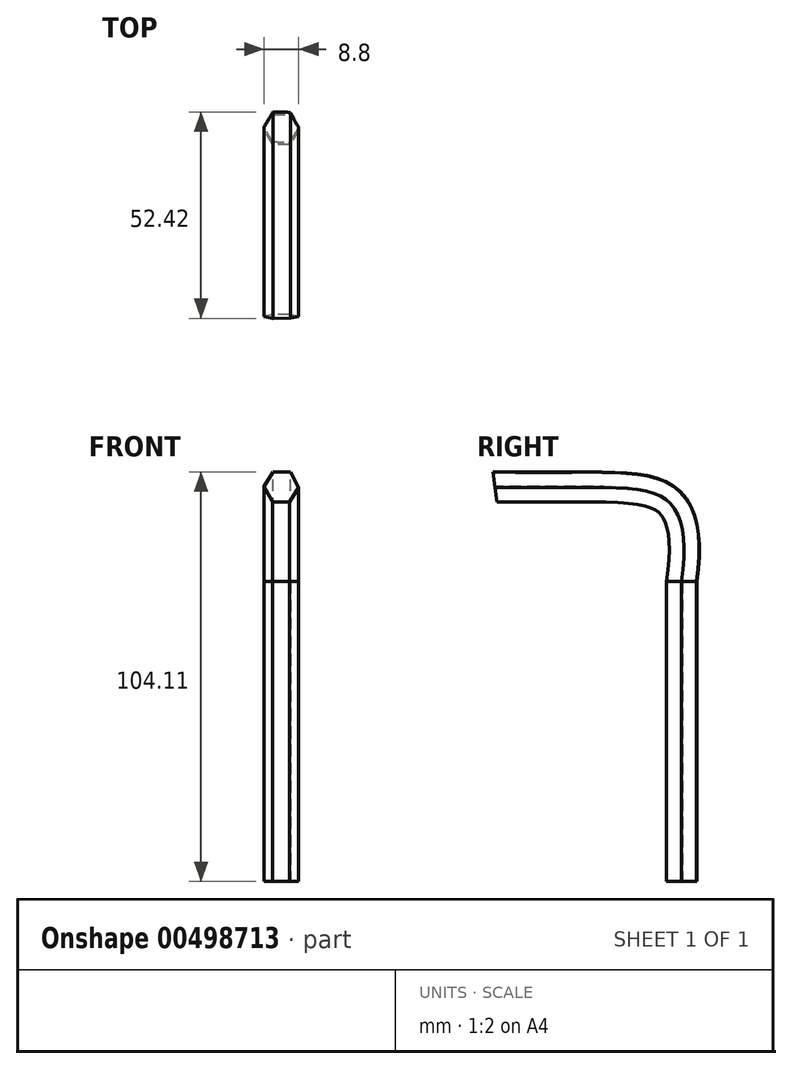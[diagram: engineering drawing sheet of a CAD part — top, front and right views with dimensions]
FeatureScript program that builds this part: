
annotation { "Feature Type Name" : "Feature", "Feature Type Description" : "" }
export const myFeature = defineFeature(function(context is Context, id is Id, definition is map)
    precondition{}
    {
        {
            var Q0;
            Q0=qCreatedBy(makeId("Top.planeOp"),FACE);
            var sketch = newSketch(context, id + "F0", { "sketchPlane" : qUnion([Q0])});
            skCircle(sketch, "E0.cCircle", {"center": v(-8.9, 61.26) * mm, "radius": 3.81 * mm, "construction": true});
            skLineSegment(sketch, "E0.0", {"start": v(-4.5, 61.16) * mm, "end": v(-6.78, 57.4) * mm});
            skLineSegment(sketch, "E0.1", {"start": v(-6.78, 57.4) * mm, "end": v(-11.18, 57.5) * mm});
            skLineSegment(sketch, "E0.2", {"start": v(-11.18, 57.5) * mm, "end": v(-13.29, 61.36) * mm});
            skLineSegment(sketch, "E0.3", {"start": v(-13.29, 61.36) * mm, "end": v(-11, 65.12) * mm});
            skLineSegment(sketch, "E0.4", {"start": v(-11, 65.12) * mm, "end": v(-6.6, 65.02) * mm});
            skLineSegment(sketch, "E0.5", {"start": v(-6.6, 65.02) * mm, "end": v(-4.5, 61.16) * mm});
            skPoint(sketch, "E0.0.midPoint", {"position": v(-5.64, 59.28) * mm});
            skSolve(sketch);
        }
        {
            var Q0;
            Q0 = qSketchRegion(id + "F0", true);
            extrude(context, id + "F1", {"entities" : qUnion([Q0]), "depth" : 76.2 * mm, "offsetDistance" : 25.4 * mm});
        }
        {
            var Q0;
            Q0=qCreatedBy(makeId("Right.planeOp"),FACE);
            var sketch = newSketch(context, id + "F2", { "sketchPlane" : qUnion([Q0])});
            skLineSegment(sketch, "E1.0.0", {"start": v(61.16, 76.2) * mm, "end": v(65.02, 76.2) * mm});
            skLineSegment(sketch, "E1.0.1", {"start": v(65.02, 76.2) * mm, "end": v(65.12, 76.2) * mm});
            skLineSegment(sketch, "E1.0.2", {"start": v(65.12, 76.2) * mm, "end": v(61.36, 76.2) * mm});
            skLineSegment(sketch, "E1.0.3", {"start": v(61.36, 76.2) * mm, "end": v(57.5, 76.2) * mm});
            skLineSegment(sketch, "E1.0.4", {"start": v(57.5, 76.2) * mm, "end": v(57.4, 76.2) * mm});
            skLineSegment(sketch, "E1.0.5", {"start": v(57.4, 76.2) * mm, "end": v(61.16, 76.2) * mm});
            skFitSpline(sketch, "E2", {"points": [v(61.36, 76.2) * mm, v(58.2, 96.52) * mm, v(13.8, 100.38) * mm], "startDerivative": vector(10.48, 74.63) * mm, "endDerivative": vector(-137.11, 1.75) * mm});
            skSolve(sketch);
        }
        {
            var Q0;
            Q0=makeQuery(id+"F1.opExtrude","CAP_FACE",FACE,{"disambiguationData":[OSD([sQuery(id+"F0.wireOp",EDGE,"E0.0"),sQuery(id+"F0.wireOp",EDGE,"E0.1"),sQuery(id+"F0.wireOp",EDGE,"E0.2"),sQuery(id+"F0.wireOp",EDGE,"E0.3"),sQuery(id+"F0.wireOp",EDGE,"E0.4"),sQuery(id+"F0.wireOp",EDGE,"E0.5")])],"isStart":false});
            var Q1;
            Q1=sQuery(id+"F2.wireOp",EDGE,"E2");
            sweep(context, id + "F3", {"operationType" : NewBodyOperationType.ADD, "profiles" : qUnion([Q0]), "path" : qUnion([Q1])});
        }
    });
